# Revit family: HSW60_top_fstb_dg_Concept L_0908
name_source: partatom
category: Doors
revit_build: Autodesk Revit 2018 (Build: 20170223_1515(x64)
units: mm (PartAtom-declared; Revit-internal decimal feet)

## family parameters
Always vertical = Yes
Cut with Voids When Loaded = No
Host = Wall
OmniClass Number = 23.30.10.17.11
OmniClass Title = Sliding Doors
Room Calculation Point = No
Shared = No

## types (4) — shared parameters
04 CSI = 08 41 13
95 CSI = 8411
Analytic Construction = <None>
Assembly Code = B2030110
Cost Info = https://www.nanawall.com
Description = Single Track Sliding System
Detail Component in Plan = Yes
Detail Component in Section = Yes
Engineering Details URL = https://www.nanawall.com
Glass Material = Glass - NanaWall - Generic
Glazing Options = https://www.nanawall.com
Glazing Thickness = 24 mm  [stored 0.0787402 ft]
Height = 2743 mm
Height Constraint = 2743 mm
Installation and Service URL = https://www.nanawall.com
Jamb Height = 2767 mm
Manufacturer = NanaWall Systems, Inc.
Manufacturer Fax = (415) 383-0312
Model = HSW60 - Concept B
NanaWall Configurator = http://www.nanawall.com
Opening Width = 2915 mm
Performance URL = https://www.nanawall.com
Product Page URL = https://www.nanawall.com
Rough Height = 2743 mm
Rough Width = 3000 mm
Sash = Metal - NanaWall - Aluminum
Sills Available = Surface Mounted, Floor Sockets, Low Profile Saddle, Flush
Size Note = Adjust Height and Width as necessary to fit your project needs. Multiple Panel and opening configurations are available. See Product Page URL for more information.
Subcategory = Sliding Glass Wall
Thickness = 64 mm  [stored 0.209974 ft]
URL = http://www.nanawall.com
Wall Closure = By host
Warranty URL = http://www.nanawall.com
Width = 3048 mm  [stored 10 ft]
Width C = 3048 mm  [stored 10 ft]
not DIP = No

## per-type parameters (varying)
| type | Flush Sill | Low Profile Saddle Sill | No Sill - Floor Socket | Surface Mounted Sill |
| HSW60-Configuration_B Surface Mounted Sill | No | Yes | No | No |
| HSW60-Configuration_B Low Profile Saddle Sill | No | No | No | Yes |
| HSW60-Configuration_B Flush Sill | Yes | No | No | No |
| HSW60-Configuration_B No Sill - Floor Sockets | No | No | Yes | No |

note: [stored X ft] marks values corroborated as IEEE doubles in the binary element streams (Revit-internal decimal feet)

## geometry (parser evidence)
native form markers: Blend x1714, Sweep x53
no freeform markers — native parametric forms only
